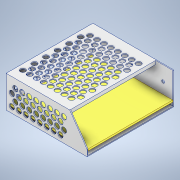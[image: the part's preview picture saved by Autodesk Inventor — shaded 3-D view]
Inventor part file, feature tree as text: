
AUTODESK INVENTOR PART (.ipt)
format: ipt  version: 2021 (Build 250183000, 183)  size: 507,904 bytes
history: native  units: mm
features: extrude x12, pattern_linear x8, sketch x5, thread x4, boolean_combine x3, other x1
ambient origin geometry x8: Origin, YZ Plane, XZ Plane, XY Plane, X Axis, Y Axis, Z Axis, Center Point
bodies: Solid1 (feature_tree), Solid2 (feature_tree), Solid4 (feature_tree), Solid5 (feature_tree), Solid6 (feature_tree), Solid8 (feature_tree), Solid9 (feature_tree)
feature tree (33):
  sketch  "Sketch1"  dims[d0=27.5mm d1=70.0mm]
  extrude  "Extrusion1"  Depth=70.0mm
  extrude  "Extrusion4"  Depth=5.5mm
  extrude  "Extrusion2"  Depth=73.5mm TaperAngle=0.0deg
  extrude  "Extrusion3"  Depth=0.75mm
  sketch  "Sketch2"  dims[d2=55.0mm d3=5.5mm]
  extrude  "Extrusion5"  Depth=0.75mm
  pattern_linear  "Rectangular Pattern1"  Spacing1=0.75mm  [1 undecoded]
  extrude  "Extrusion6"  Depth=0.5mm
  pattern_linear  "Rectangular Pattern2"  Spacing1=1.57mm  [1 undecoded]
  pattern_linear  "Rectangular Pattern3"  Spacing1=73.0mm  [1 undecoded]
  boolean_combine  "Combine1"
  sketch  "Sketch3"  dims[d4=75.0mm d5=0.0mm d6=73.5mm d7=0.0mm]
  extrude  "Extrusion7"  Depth=73.0mm TaperAngle=0.0deg
  extrude  "Extrusion8"  Depth=0.75mm
  pattern_linear  "Rectangular Pattern4"  Spacing1=4.5mm  [1 undecoded]
  boolean_combine  "Combine2"
  sketch  "Sketch4"  dims[d8=3.0mm d9=0.75mm]
  extrude  "Extrusion9"  Depth=0.75mm
  extrude  "Extrusion10"  Depth=0.75mm
  pattern_linear  "Rectangular Pattern5"  Spacing1=5.0mm  [1 undecoded]
  pattern_linear  "Rectangular Pattern6"  Spacing1=5.0mm  [1 undecoded]
  pattern_linear  "Rectangular Pattern7"  Spacing1=9.5mm  [1 undecoded]
  pattern_linear  "Rectangular Pattern8"  Spacing1=73.0mm  [1 undecoded]
  boolean_combine  "Combine3"
  other  "Power Supply Side Mount"
  extrude  "Extrusion11"  Depth=0.75mm
  thread  "Thread1"  [1 undecoded]
  thread  "Thread2"  [1 undecoded]
  extrude  "Extrusion12"  Depth=10.0mm
  thread  "Thread3"  [1 undecoded]
  thread  "Thread4"  [1 undecoded]
  sketch  "Sketch6"  dims[d10=0.75mm d11=0.75mm d12=0.75mm d13=0.5mm d14=1.57mm d15=73.0mm d16=0.0mm d17=73.0mm d18=0.0mm d19=4.5mm d20=4.5mm d21=4.5mm d23=6.0mm d24=5.0mm d25=5.0mm d26=9.5mm d27=73.0mm d28=0.0mm d29=80.0mm d31=6.0mm d32=73.0mm d33=0.0mm d34=80.0mm d36=6.0mm d37=60.0mm d39=10.0mm d40=4.5mm d41=4.5mm d42=4.5mm d43=6.0mm d44=5.0mm d45=5.0mm d46=5.0mm d47=73.0mm d48=0.0mm d49=73.0mm d50=0.0mm d51=80.0mm d53=6.0mm d54=20.0mm d56=10.0mm d57=4.5mm d58=4.5mm d59=4.5mm d60=10.0mm d61=3.0mm d62=9.0mm d63=7.5mm d64=73.0mm d65=0.0mm d66=73.0mm d67=0.0mm d68=30.0mm d70=6.0mm d71=60.0mm d73=10.0mm d74=20.0mm d76=6.0mm d77=50.0mm d79=10.0mm d80=2.5mm d81=2.5mm d82=12.5mm d83=34.0mm d85=73.0mm d86=0.0mm d87=0.75mm d88=0.0mm d89=0.75mm d90=0.0mm d91=37.0mm d92=2.5mm d93=2.5mm d94=4.0mm d95=50.0mm d96=73.0mm d97=0.0mm d98=0.75mm d99=0.0mm d100=0.75mm d101=0.0mm]
note: 12 required parameter values undecoded (feature->parameter linkage not recoverable at this tier; creation-order binding heuristic only, values carry confidence <= 0.55)
